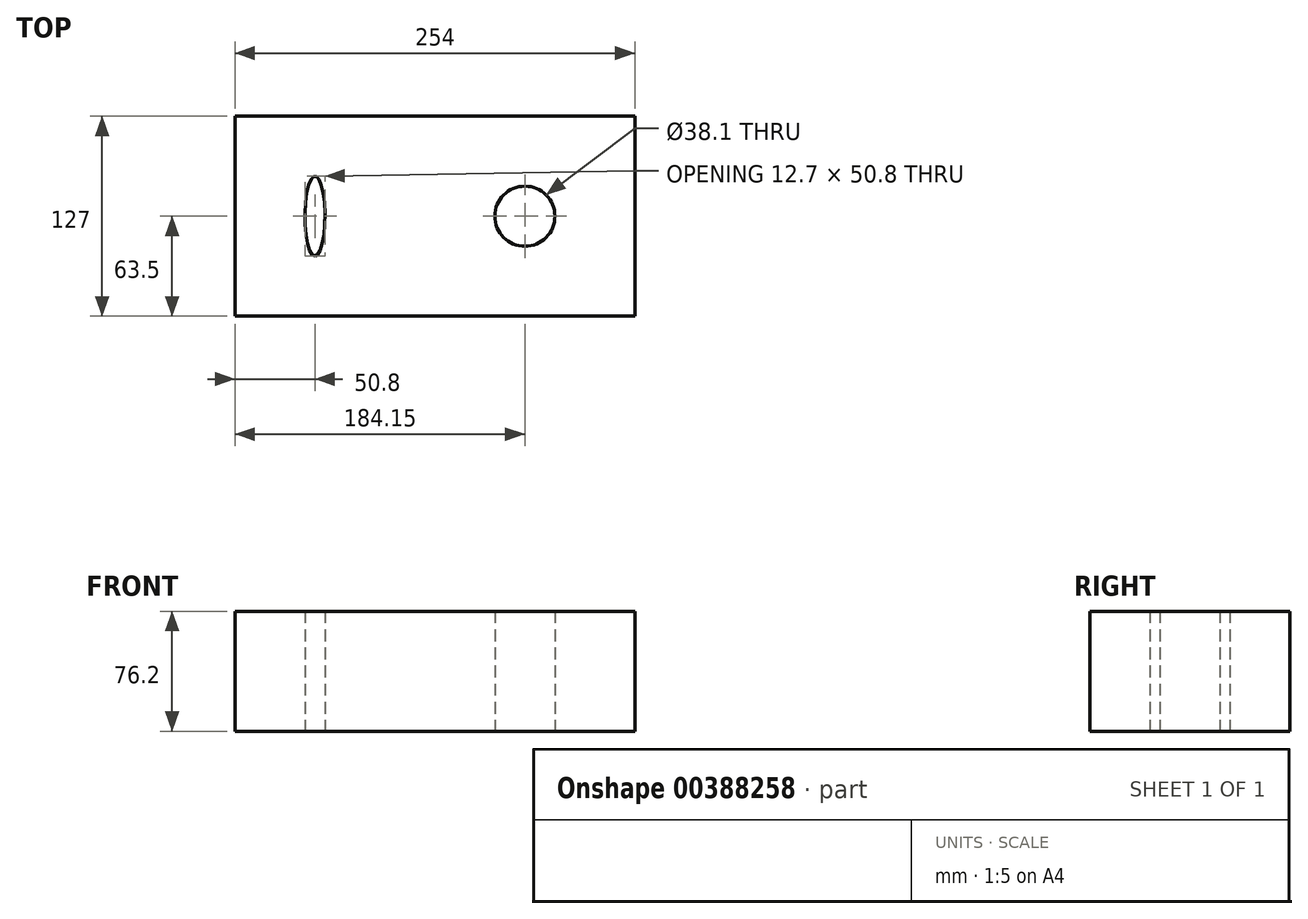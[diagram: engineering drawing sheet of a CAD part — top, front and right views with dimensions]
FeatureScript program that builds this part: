
annotation { "Feature Type Name" : "Feature", "Feature Type Description" : "" }
export const myFeature = defineFeature(function(context is Context, id is Id, definition is map)
    precondition{}
    {
        {
            var Q0;
            Q0=qCreatedBy(makeId("Top.planeOp"),FACE);
            var sketch = newSketch(context, id + "F0", { "sketchPlane" : qUnion([Q0])});
            skLineSegment(sketch, "E0.bottom", {"start": v(0, 0) * mm, "end": v(254, 0) * mm});
            skLineSegment(sketch, "E0.top", {"start": v(0, 127) * mm, "end": v(254, 127) * mm});
            skLineSegment(sketch, "E0.left", {"start": v(0, 0) * mm, "end": v(0, 127) * mm});
            skLineSegment(sketch, "E0.right", {"start": v(254, 0) * mm, "end": v(254, 127) * mm});
            skSolve(sketch);
        }
        {
            var Q0;
            Q0=makeQuery(id+"F0.imprint","IMPRINT",FACE,{"disambiguationData":[TD([[makeQuery(id+"F0.imprint","IMPRINT",EDGE,{"derivedFrom":sQuery(id+"F0.wireOp",EDGE,"E0.bottom")}),1.0]])]});
            extrude(context, id + "F1", {"entities" : qUnion([Q0]), "depth" : 76.2 * mm});
        }
        {
            var Q0;
            Q0=qCreatedBy(makeId("Top.planeOp"),FACE);
            var sketch = newSketch(context, id + "F2", { "sketchPlane" : qUnion([Q0])});
            skCircle(sketch, "E1", {"center": v(184.15, 63.5) * mm, "radius": 19.05 * mm});
            skSolve(sketch);
        }
        {
            var Q0;
            Q0=qCreatedBy(makeId("Top.planeOp"),FACE);
            var sketch = newSketch(context, id + "F3", { "sketchPlane" : qUnion([Q0])});
            skEllipse(sketch, "E2", {"center": v(50.8, 63.5) * mm, "majorRadius": 25.4 * mm, "minorRadius": 6.35 * mm, "majorAxis": v(0, -1)});
            skSolve(sketch);
        }
        {
            var Q0;
            Q0=makeQuery(id+"F3.imprint","IMPRINT",FACE,{"disambiguationData":[TD([[makeQuery(id+"F3.imprint","IMPRINT",EDGE,{"derivedFrom":sQuery(id+"F3.wireOp",EDGE,"E2")}),1.0]])]});
            var Q1;
            Q1=sQuery(id+"F3.wireOp",EDGE,"E2");
            extrude(context, id + "F4", {"entities" : qUnion([Q0]), "operationType" : NewBodyOperationType.REMOVE, "surfaceEntities" : qUnion([Q1]), "endBound" : BoundingType.THROUGH_ALL, "depth" : 487.17 * mm});
        }
        {
            var Q0;
            Q0=makeQuery(id+"F2.imprint","IMPRINT",FACE,{"disambiguationData":[TD([[makeQuery(id+"F2.imprint","IMPRINT",EDGE,{"derivedFrom":sQuery(id+"F2.wireOp",EDGE,"E1")}),1.0]])]});
            extrude(context, id + "F5", {"entities" : qUnion([Q0]), "operationType" : NewBodyOperationType.REMOVE, "depth" : 279.4 * mm});
        }
    });
